# Revit family: Safety-Railing_Section_SafetyRail_Mobile-InPlantSwingGate
name_source: partatom
category: Railings
units: mm (PartAtom-declared; Revit-internal decimal feet)

## family parameters
Classification Number = 23.30.80.11
Cut with Voids When Loaded = No
Shared = No

## types (3) — shared parameters
Base Weight = 104 lbs per Base Plate
Clear Opening Width = 0' - 0"
Construction Details = http://www.arcat.com
Description = Safety Rail Company Mobile In-Plant Swing Safety Gate as Specified
Green Building-LEED = http://www.arcat.com
Height Adjustment Required = 0' - 0"
Keynote = 05 52 00
Manufacturer = Safety Rail Company
Manufacturer Fax = 888-471-4931
Manufacturer Website = http://www.safetyrailcompany.com
Model = Mobile In-Plant Swing Safety Gate
Post OD = 0' - 1 5/8"
Product Data = http://www.arcat.com
Product Properties = http://www.safetyrailcompany.com
Revision = R1_2017-08
Sales Information = http://www.safetyrailcompany.com
SpecWizard = http://www.arcat.com
Specification = http://www.arcat.com
Standards Conformance = OSHA Guardrail Reg 1910.23, 1926.500 - .503  ;  Made in USA
URL = http://www.safetyrailcompany.com
Unit Height = 3' - 7 11/16"
zero-valued in all types: Expected Lifespan (Years), Maintenance Schedule (Months), Warranty Duration (Years)

## per-type parameters (varying)
| type | Unit Length |
| 10 ft | 10' - 0" |
| 5 ft | 5' - 0" |
| 3 ft | 3' - 0" |

## geometry (parser evidence)
native form markers: Sweep x7
no freeform markers — native parametric forms only
